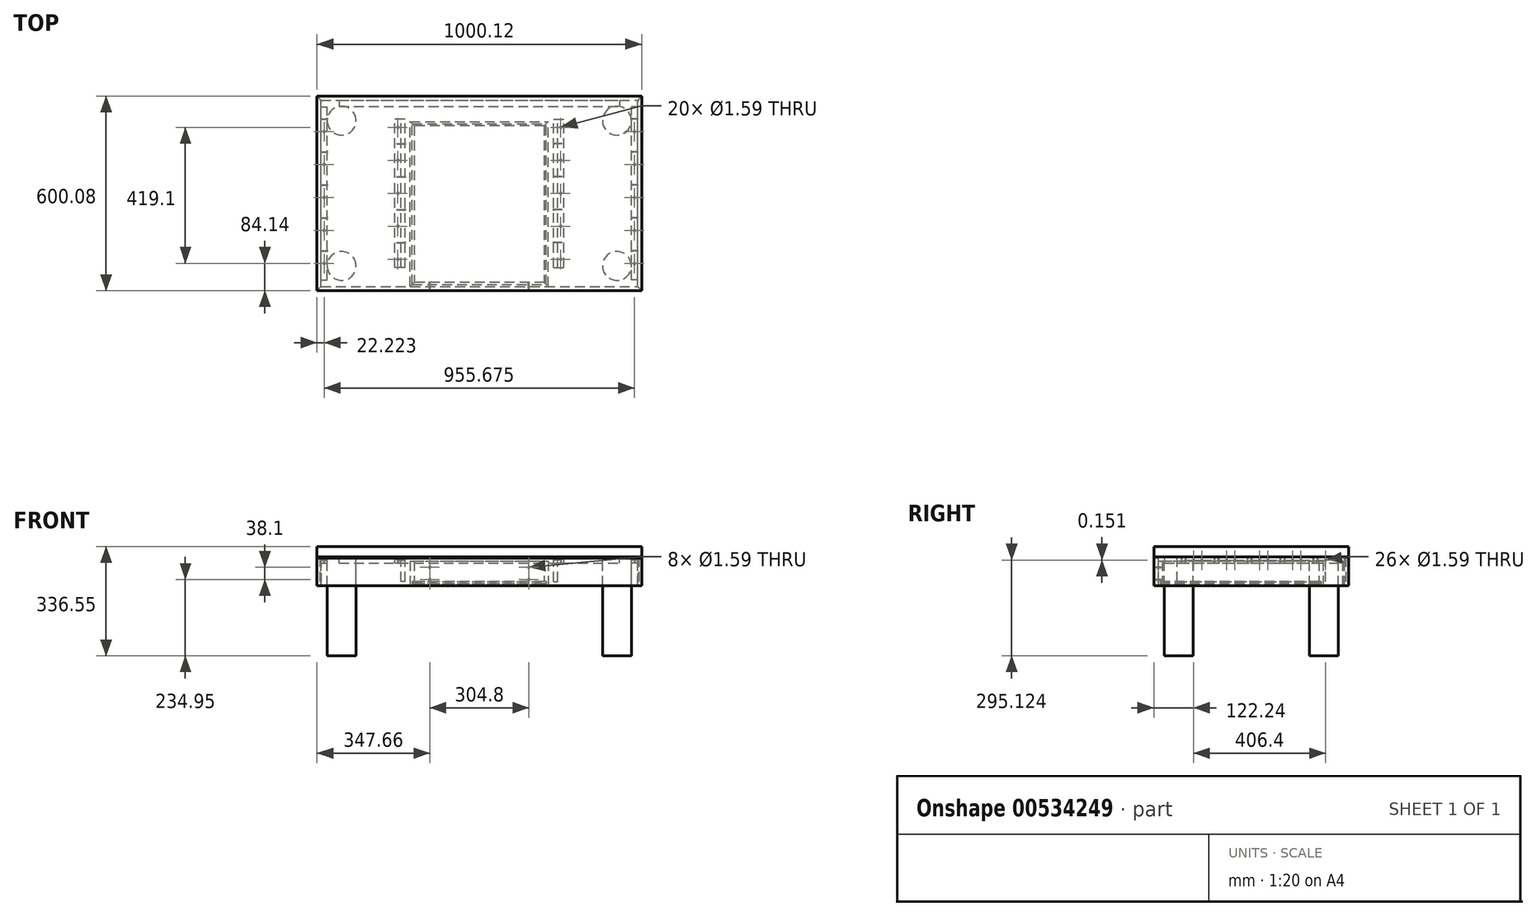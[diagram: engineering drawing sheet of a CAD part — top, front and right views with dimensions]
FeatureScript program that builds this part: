
annotation { "Feature Type Name" : "Feature", "Feature Type Description" : "" }
export const myFeature = defineFeature(function(context is Context, id is Id, definition is map)
    precondition{}
    {
        {
            var Q0;
            Q0=qCreatedBy(makeId("Top.planeOp"),FACE);
            var sketch = newSketch(context, id + "F0", { "sketchPlane" : qUnion([Q0])});
            skLineSegment(sketch, "E0.bottom", {"start": v(-500.06, 300.04) * mm, "end": v(500.06, 300.04) * mm});
            skLineSegment(sketch, "E0.top", {"start": v(-500.06, -300.04) * mm, "end": v(500.06, -300.04) * mm});
            skLineSegment(sketch, "E0.left", {"start": v(-500.06, 300.04) * mm, "end": v(-500.06, -300.04) * mm});
            skLineSegment(sketch, "E0.right", {"start": v(500.06, 300.04) * mm, "end": v(500.06, -300.04) * mm});
            skSolve(sketch);
        }
        {
            var Q0;
            Q0=makeQuery(id+"F0.imprint","IMPRINT",FACE,{"disambiguationData":[TD([[makeQuery(id+"F0.imprint","IMPRINT",EDGE,{"derivedFrom":sQuery(id+"F0.wireOp",EDGE,"E0.bottom")}),-1.0]])]});
            extrude(context, id + "F1", {"entities" : qUnion([Q0]), "depth" : 31.75 * mm, "offsetDistance" : 25.4 * mm});
        }
        {
            var Q0;
            Q0=makeQuery(id+"F1.opExtrude","CAP_FACE",FACE,{"disambiguationData":[OSD([sQuery(id+"F0.wireOp",EDGE,"E0.bottom"),sQuery(id+"F0.wireOp",EDGE,"E0.top"),sQuery(id+"F0.wireOp",EDGE,"E0.left"),sQuery(id+"F0.wireOp",EDGE,"E0.right")])],"isStart":true});
            var sketch = newSketch(context, id + "F2", { "sketchPlane" : qUnion([Q0])});
            skCircle(sketch, "E1", {"center": v(-423.86, 223.84) * mm, "radius": 44.45 * mm});
            skLineSegment(sketch, "E2", {"start": v(-423.86, 223.84) * mm, "end": v(-500.06, 223.84) * mm, "construction": true});
            skLineSegment(sketch, "E3", {"start": v(-423.86, 223.84) * mm, "end": v(-423.86, 300.04) * mm, "construction": true});
            skCircle(sketch, "E4", {"center": v(-423.86, -223.84) * mm, "radius": 44.45 * mm});
            skCircle(sketch, "E5", {"center": v(423.86, -223.84) * mm, "radius": 44.45 * mm});
            skCircle(sketch, "E6", {"center": v(423.86, 223.84) * mm, "radius": 44.45 * mm});
            skLineSegment(sketch, "E7", {"start": v(423.86, 223.84) * mm, "end": v(423.86, 300.04) * mm, "construction": true});
            skLineSegment(sketch, "E8", {"start": v(423.86, 223.84) * mm, "end": v(500.06, 223.84) * mm, "construction": true});
            skLineSegment(sketch, "E9", {"start": v(423.86, -223.84) * mm, "end": v(500.06, -223.84) * mm, "construction": true});
            skLineSegment(sketch, "E10", {"start": v(-500.06, -223.84) * mm, "end": v(-423.86, -223.84) * mm, "construction": true});
            skLineSegment(sketch, "E11", {"start": v(-423.86, -300.04) * mm, "end": v(-423.86, -223.84) * mm, "construction": true});
            skLineSegment(sketch, "E12", {"start": v(423.86, -223.84) * mm, "end": v(423.86, -300.04) * mm, "construction": true});
            skSolve(sketch);
        }
        {
            var Q0;
            Q0=makeQuery(id+"F2.imprint","IMPRINT",FACE,{"disambiguationData":[TD([[makeQuery(id+"F2.imprint","IMPRINT",EDGE,{"derivedFrom":sQuery(id+"F2.wireOp",EDGE,"E1")}),1.0]])]});
            var Q1;
            Q1=makeQuery(id+"F2.imprint","IMPRINT",FACE,{"disambiguationData":[TD([[makeQuery(id+"F2.imprint","IMPRINT",EDGE,{"derivedFrom":sQuery(id+"F2.wireOp",EDGE,"E6")}),1.0]])]});
            var Q2;
            Q2=makeQuery(id+"F2.imprint","IMPRINT",FACE,{"disambiguationData":[TD([[makeQuery(id+"F2.imprint","IMPRINT",EDGE,{"derivedFrom":sQuery(id+"F2.wireOp",EDGE,"E5")}),1.0]])]});
            var Q3;
            Q3=makeQuery(id+"F2.imprint","IMPRINT",FACE,{"disambiguationData":[TD([[makeQuery(id+"F2.imprint","IMPRINT",EDGE,{"derivedFrom":sQuery(id+"F2.wireOp",EDGE,"E4")}),1.0]])]});
            extrude(context, id + "F3", {"entities" : qUnion([Q0, Q1, Q2, Q3]), "operationType" : NewBodyOperationType.ADD, "depth" : 304.8 * mm, "offsetDistance" : 25.4 * mm});
        }
        {
            var Q0;
            Q0=makeQuery(id+"F1.opExtrude","CAP_FACE",FACE,{"disambiguationData":[OSD([sQuery(id+"F0.wireOp",EDGE,"E0.bottom"),sQuery(id+"F0.wireOp",EDGE,"E0.top"),sQuery(id+"F0.wireOp",EDGE,"E0.left"),sQuery(id+"F0.wireOp",EDGE,"E0.right")])],"isStart":true});
            var sketch = newSketch(context, id + "F4", { "sketchPlane" : qUnion([Q0])});
            skLineSegment(sketch, "E13.bottom", {"start": v(-500.06, 300.04) * mm, "end": v(-487.36, 300.04) * mm});
            skLineSegment(sketch, "E13.left", {"start": v(-500.06, 300.04) * mm, "end": v(-500.06, -300.04) * mm});
            skLineSegment(sketch, "E13.right", {"start": v(-487.36, 300.04) * mm, "end": v(-487.36, -287.34) * mm});
            skLineSegment(sketch, "E14.bottom", {"start": v(-487.36, 266.7) * mm, "end": v(-468.31, 266.7) * mm});
            skLineSegment(sketch, "E14.top", {"start": v(-487.36, -266.7) * mm, "end": v(-468.31, -266.7) * mm});
            skLineSegment(sketch, "E14.left", {"start": v(-487.36, 266.7) * mm, "end": v(-487.36, -266.7) * mm});
            skLineSegment(sketch, "E14.right", {"start": v(-468.31, 266.7) * mm, "end": v(-468.31, -266.7) * mm});
            skLineSegment(sketch, "E15.bottom", {"start": v(-228.6, 228.6) * mm, "end": v(-241.3, 228.6) * mm});
            skLineSegment(sketch, "E15.top", {"start": v(-228.6, -228.6) * mm, "end": v(-241.3, -228.6) * mm});
            skLineSegment(sketch, "E15.left", {"start": v(-228.6, 228.6) * mm, "end": v(-228.6, -228.6) * mm});
            skLineSegment(sketch, "E15.right", {"start": v(-241.3, 228.6) * mm, "end": v(-241.3, -228.6) * mm});
            skLineSegment(sketch, "E16.bottom", {"start": v(-241.3, 228.6) * mm, "end": v(-260.35, 228.6) * mm});
            skLineSegment(sketch, "E16.top", {"start": v(-241.3, -228.6) * mm, "end": v(-260.35, -228.6) * mm});
            skLineSegment(sketch, "E16.right", {"start": v(-260.35, 228.6) * mm, "end": v(-260.35, -228.6) * mm});
            skLineSegment(sketch, "E17.bottom", {"start": v(-500.06, -300.04) * mm, "end": v(500.06, -300.04) * mm});
            skLineSegment(sketch, "E17.top", {"start": v(-487.36, -287.34) * mm, "end": v(487.36, -287.34) * mm});
            skLineSegment(sketch, "E18", {"start": v(-500.06, -300.04) * mm, "end": v(-487.36, -287.34) * mm});
            skLineSegment(sketch, "E19", {"start": v(500.06, -300.04) * mm, "end": v(487.36, -287.34) * mm});
            skSolve(sketch);
        }
        {
            var Q0;
            Q0=makeQuery(id+"F4.imprint","IMPRINT",FACE,{"disambiguationData":[TD([[makeQuery(id+"F4.imprint","IMPRINT",EDGE,{"derivedFrom":sQuery(id+"F4.wireOp",EDGE,"E13.bottom")}),-1.0]])]});
            extrude(context, id + "F5", {"entities" : qUnion([Q0]), "depth" : 88.9 * mm, "offsetDistance" : 25.4 * mm});
        }
        {
            var Q0;
            Q0=makeQuery(id+"F4.imprint","IMPRINT",FACE,{"disambiguationData":[TD([[makeQuery(id+"F4.imprint","IMPRINT",EDGE,{"derivedFrom":sQuery(id+"F4.wireOp",EDGE,"E14.bottom")}),-1.0]])]});
            extrude(context, id + "F6", {"entities" : qUnion([Q0]), "depth" : 19.05 * mm, "offsetDistance" : 25.4 * mm});
        }
        {
            var Q0;
            Q0=makeQuery(id+"F4.imprint","IMPRINT",FACE,{"disambiguationData":[TD([[makeQuery(id+"F4.imprint","IMPRINT",EDGE,{"derivedFrom":sQuery(id+"F4.wireOp",EDGE,"E17.bottom")}),1.0]])]});
            extrude(context, id + "F7", {"entities" : qUnion([Q0]), "depth" : 88.9 * mm, "offsetDistance" : 25.4 * mm});
        }
        {
            var Q0;
            Q0=makeQuery(id+"F4.imprint","IMPRINT",FACE,{"disambiguationData":[TD([[makeQuery(id+"F4.imprint","IMPRINT",EDGE,{"derivedFrom":sQuery(id+"F4.wireOp",EDGE,"E16.bottom")}),1.0]])]});
            extrude(context, id + "F8", {"entities" : qUnion([Q0]), "depth" : 19.05 * mm, "offsetDistance" : 25.4 * mm});
        }
        {
            var Q0;
            {var subQ1=sQuery(id+"F4.wireOp",EDGE,"E15.bottom");Q0=makeQuery(id+"F4.imprint","IMPRINT",FACE,{"disambiguationData":[TD([[makeQuery(id+"F4.imprint","IMPRINT",EDGE,{"derivedFrom":subQ1}),1.0]])]});}
            var Q1;
            Q1=makeQuery(id+"F5.opExtrude","CAP_FACE",FACE,{"disambiguationData":[OSD([sQuery(id+"F4.wireOp",EDGE,"E13.bottom"),sQuery(id+"F4.wireOp",EDGE,"E13.top"),sQuery(id+"F4.wireOp",EDGE,"E13.left"),sQuery(id+"F4.wireOp",EDGE,"E13.right"),sQuery(id+"F4.wireOp",EDGE,"E14.left")])],"isStart":false});
            extrude(context, id + "F9", {"entities" : qUnion([Q0]), "endBound" : BoundingType.UP_TO_SURFACE, "depth" : 69.85 * mm, "endBoundEntityFace" : qUnion([Q1]), "hasOffset" : true, "offsetDistance" : 12.7 * mm});
        }
        {
            var Q0;
            Q0=makeQuery(id+"F8.opExtrude","CAP_FACE",FACE,{"disambiguationData":[OSD([sQuery(id+"F4.wireOp",EDGE,"E16.bottom"),sQuery(id+"F4.wireOp",EDGE,"E16.top"),sQuery(id+"F4.wireOp",EDGE,"E15.right"),sQuery(id+"F4.wireOp",EDGE,"E16.right")])],"isStart":false});
            var sketch = newSketch(context, id + "F10", { "sketchPlane" : qUnion([Q0])});
            skPoint(sketch, "E20", {"position": v(-250.83, -203.2) * mm});
            skPoint(sketch, "E20.positionSnap0", {"position": v(-250.83, -228.6) * mm});
            skPoint(sketch, "E21.0.1.0", {"position": v(-250.83, -101.6) * mm});
            skPoint(sketch, "E21.0.2.0", {"position": v(-250.83, 0) * mm});
            skPoint(sketch, "E21.0.3.0", {"position": v(-250.83, 101.6) * mm});
            skLineSegment(sketch, "E21.direction1", {"start": v(-250.83, -203.2) * mm, "end": v(-225.43, -203.2) * mm, "construction": true});
            skLineSegment(sketch, "E21.direction2", {"start": v(-250.83, -203.2) * mm, "end": v(-250.83, -101.6) * mm, "construction": true});
            skPoint(sketch, "E22.0.0.4", {"position": v(-250.83, 203.2) * mm});
            skSolve(sketch);
        }
        {
            var Q0;
            Q0=makeQuery(id+"F9.opExtrude","SWEPT_FACE",FACE,{"disambiguationData":[OSD([sQuery(id+"F4.wireOp",EDGE,"E15.left")])]});
            var sketch = newSketch(context, id + "F11", { "sketchPlane" : qUnion([Q0])});
            skLineSegment(sketch, "E23", {"start": v(228.6, -9.68) * mm, "end": v(-228.6, -9.68) * mm, "construction": true});
            skPoint(sketch, "E24", {"position": v(152.4, -9.68) * mm});
            skPoint(sketch, "E25.1.0.0", {"position": v(50.8, -9.68) * mm});
            skPoint(sketch, "E25.2.0.0", {"position": v(-50.8, -9.68) * mm});
            skPoint(sketch, "E25.3.0.0", {"position": v(-152.4, -9.68) * mm});
            skLineSegment(sketch, "E25.direction1", {"start": v(152.4, -9.68) * mm, "end": v(50.8, -9.68) * mm, "construction": true});
            skSolve(sketch);
        }
        {
            var Q0;
            Q0=makeQuery(id+"F6.opExtrude","CAP_FACE",FACE,{"disambiguationData":[OSD([sQuery(id+"F4.wireOp",EDGE,"E14.bottom"),sQuery(id+"F4.wireOp",EDGE,"E14.top"),sQuery(id+"F4.wireOp",EDGE,"E14.left"),sQuery(id+"F4.wireOp",EDGE,"E14.right")])],"isStart":false});
            var sketch = newSketch(context, id + "F12", { "sketchPlane" : qUnion([Q0])});
            skPoint(sketch, "E26", {"position": v(-477.84, -190.5) * mm});
            skPoint(sketch, "E26.positionSnap0", {"position": v(-477.84, -266.7) * mm});
            skPoint(sketch, "E27.0.1.0", {"position": v(-477.84, -88.9) * mm});
            skPoint(sketch, "E27.0.2.0", {"position": v(-477.84, 12.7) * mm});
            skPoint(sketch, "E27.0.3.0", {"position": v(-477.84, 114.3) * mm});
            skPoint(sketch, "E27.0.4.0", {"position": v(-477.84, 215.9) * mm});
            skLineSegment(sketch, "E27.direction1", {"start": v(-477.84, -266.7) * mm, "end": v(-452.44, -266.7) * mm, "construction": true});
            skLineSegment(sketch, "E27.direction2", {"start": v(-477.84, -266.7) * mm, "end": v(-477.84, -114.3) * mm, "construction": true});
            skSolve(sketch);
        }
        {
            var Q0;
            Q0=makeQuery(id+"F6.opExtrude","SWEPT_FACE",FACE,{"disambiguationData":[OSD([sQuery(id+"F4.wireOp",EDGE,"E14.right")])]});
            var sketch = newSketch(context, id + "F13", { "sketchPlane" : qUnion([Q0])});
            skPoint(sketch, "E28", {"position": v(228.6, -9.52) * mm});
            skPoint(sketch, "E28.positionSnap0", {"position": v(266.7, -9.53) * mm});
            skPoint(sketch, "E29.1.0.0", {"position": v(127, -9.53) * mm});
            skPoint(sketch, "E29.2.0.0", {"position": v(25.4, -9.53) * mm});
            skPoint(sketch, "E29.3.0.0", {"position": v(-76.2, -9.53) * mm});
            skPoint(sketch, "E29.4.0.0", {"position": v(-177.8, -9.53) * mm});
            skLineSegment(sketch, "E29.direction1", {"start": v(228.6, -9.53) * mm, "end": v(127, -9.53) * mm, "construction": true});
            skSolve(sketch);
        }
        {
            var Q0;
            Q0=sQuery(id+"F10.wireOp",VERTEX,"E20");
            var Q1;
            Q1=sQuery(id+"F10.wireOp",VERTEX,"E21.0.1.0");
            var Q2;
            Q2=sQuery(id+"F10.wireOp",VERTEX,"E21.0.2.0");
            var Q3;
            Q3=sQuery(id+"F10.wireOp",VERTEX,"E21.0.3.0");
            var Q4;
            Q4=sQuery(id+"F10.wireOp",VERTEX,"E21.0.4.0");
            var Q5;
            Q5=sQuery(id+"F10.wireOp",VERTEX,"E21.0.5.0");
            var Q6;
            Q6=sQuery(id+"F10.wireOp",VERTEX,"E21.0.6.0");
            var Q7;
            Q7=sQuery(id+"F10.wireOp",VERTEX,"E21.0.7.0");
            var Q8;
            Q8=sQuery(id+"F10.wireOp",VERTEX,"E21.0.8.0");
            var Q9;
            Q9=sQuery(id+"F11.wireOp",VERTEX,"E24");
            var Q10;
            Q10=sQuery(id+"F11.wireOp",VERTEX,"E25.1.0.0");
            var Q11;
            Q11=sQuery(id+"F11.wireOp",VERTEX,"E25.2.0.0");
            var Q12;
            Q12=sQuery(id+"F11.wireOp",VERTEX,"E25.3.0.0");
            var Q13;
            Q13=sQuery(id+"F11.wireOp",VERTEX,"E25.4.0.0");
            var Q14;
            Q14=sQuery(id+"F11.wireOp",VERTEX,"E25.5.0.0");
            var Q15;
            Q15=sQuery(id+"F11.wireOp",VERTEX,"E25.6.0.0");
            var Q16;
            Q16=sQuery(id+"F11.wireOp",VERTEX,"E25.7.0.0");
            var Q17;
            Q17=sQuery(id+"F10.wireOp",VERTEX,"E22.0.0.4");
            var Q18;
            Q18=sQuery(id+"F12.wireOp",VERTEX,"E26");
            var Q19;
            Q19=sQuery(id+"F12.wireOp",VERTEX,"E27.0.1.0");
            var Q20;
            Q20=sQuery(id+"F12.wireOp",VERTEX,"E27.0.2.0");
            var Q21;
            Q21=sQuery(id+"F12.wireOp",VERTEX,"E27.0.3.0");
            var Q22;
            Q22=sQuery(id+"F12.wireOp",VERTEX,"E27.0.4.0");
            var Q23;
            Q23=sQuery(id+"F13.wireOp",VERTEX,"cb4e85ae-bc8c-472d-8e2a-263fc974a90b.0.6.0");
            var Q24;
            Q24=sQuery(id+"F13.wireOp",VERTEX,"E29.5.0.0");
            var Q25;
            Q25=sQuery(id+"F13.wireOp",VERTEX,"E29.4.0.0");
            var Q26;
            Q26=sQuery(id+"F13.wireOp",VERTEX,"E29.3.0.0");
            var Q27;
            Q27=sQuery(id+"F13.wireOp",VERTEX,"E29.2.0.0");
            var Q28;
            Q28=sQuery(id+"F13.wireOp",VERTEX,"E29.1.0.0");
            var Q29;
            Q29=sQuery(id+"F13.wireOp",VERTEX,"E28");
            var Q30;
            Q30=makeQuery(id+"F8.opExtrude","SWEPT_BODY",BODY,{"disambiguationData":[OSD([sQuery(id+"F4.wireOp",EDGE,"E16.bottom"),sQuery(id+"F4.wireOp",EDGE,"E16.top"),sQuery(id+"F4.wireOp",EDGE,"E15.right"),sQuery(id+"F4.wireOp",EDGE,"E16.right")])]});
            var Q31;
            Q31=makeQuery(id+"F9.opExtrude","SWEPT_BODY",BODY,{"disambiguationData":[OSD([sQuery(id+"F4.wireOp",EDGE,"E15.bottom"),sQuery(id+"F4.wireOp",EDGE,"E15.top"),sQuery(id+"F4.wireOp",EDGE,"E15.left"),sQuery(id+"F4.wireOp",EDGE,"E15.right")])]});
            var Q32;
            Q32=makeQuery(id+"F6.opExtrude","SWEPT_BODY",BODY,{"disambiguationData":[OSD([sQuery(id+"F4.wireOp",EDGE,"E14.bottom"),sQuery(id+"F4.wireOp",EDGE,"E14.top"),sQuery(id+"F4.wireOp",EDGE,"E14.left"),sQuery(id+"F4.wireOp",EDGE,"E14.right")])]});
            hole(context, id + "F14", {"style" : HoleStyle.C_SINK, "endStyle" : HoleEndStyle.BLIND, "holeDiameter" : 1.59 * mm, "cSinkDiameter" : 6.35 * mm, "cSinkAngle" : 90 * degree, "majorDiameter" : 6.35 * mm, "holeDepth" : 25.4 * mm, "isTappedThrough" : true, "tappedDepth" : 12.7 * mm, "tapClearance" : 3, "locations" : qUnion([Q0, Q1, Q2, Q3, Q4, Q5, Q6, Q7, Q8, Q9, Q10, Q11, Q12, Q13, Q14, Q15, Q16, Q17, Q18, Q19, Q20, Q21, Q22, Q23, Q24, Q25, Q26, Q27, Q28, Q29]), "scope" : qUnion([Q30, Q31, Q32])});
        }
        {
            var Q0;
            Q0=makeQuery(id+"F5.opExtrude","SWEPT_EDGE",EDGE,{"disambiguationData":[OSD([sQuery(id+"F0.wireOp",EDGE,"E0.top"),sQuery(id+"F4.wireOp",EDGE,"E13.bottom"),sQuery(id+"F4.wireOp",EDGE,"E13.right")])]});
            var Q1;
            Q1=makeQuery(id+"F5.opExtrude","SWEPT_EDGE",EDGE,{"disambiguationData":[OSD([sQuery(id+"F0.wireOp",EDGE,"E0.bottom"),sQuery(id+"F4.wireOp",EDGE,"E13.top"),sQuery(id+"F4.wireOp",EDGE,"E13.right")])]});
            chamfer(context, id + "F15", {"entities" : qUnion([Q0, Q1]), "width" : 12.7 * mm, "tangentPropagation" : true});
        }
        {
            var Q0;
            Q0=makeQuery(id+"F5.opExtrude","SWEPT_BODY",BODY,{"disambiguationData":[OSD([sQuery(id+"F4.wireOp",EDGE,"E13.bottom"),sQuery(id+"F4.wireOp",EDGE,"E13.top"),sQuery(id+"F4.wireOp",EDGE,"E13.left"),sQuery(id+"F4.wireOp",EDGE,"E13.right")])]});
            var Q1;
            Q1=makeQuery(id+"F6.opExtrude","SWEPT_BODY",BODY,{"disambiguationData":[OSD([sQuery(id+"F4.wireOp",EDGE,"E14.bottom"),sQuery(id+"F4.wireOp",EDGE,"E14.top"),sQuery(id+"F4.wireOp",EDGE,"E14.left"),sQuery(id+"F4.wireOp",EDGE,"E14.right")])]});
            var Q2;
            Q2=makeQuery(id+"F9.opExtrude","SWEPT_BODY",BODY,{"disambiguationData":[OSD([sQuery(id+"F4.wireOp",EDGE,"E15.bottom"),sQuery(id+"F4.wireOp",EDGE,"E15.top"),sQuery(id+"F4.wireOp",EDGE,"E15.left"),sQuery(id+"F4.wireOp",EDGE,"E15.right")])]});
            var Q3;
            Q3=makeQuery(id+"F8.opExtrude","SWEPT_BODY",BODY,{"disambiguationData":[OSD([sQuery(id+"F4.wireOp",EDGE,"E16.bottom"),sQuery(id+"F4.wireOp",EDGE,"E16.top"),sQuery(id+"F4.wireOp",EDGE,"E15.right"),sQuery(id+"F4.wireOp",EDGE,"E16.right")])]});
            var Q4;
            Q4=qCreatedBy(makeId("Right.planeOp"),FACE);
            mirror(context, id + "F16", {"entities" : qUnion([Q0, Q1, Q2, Q3]), "mirrorPlane" : qUnion([Q4])});
        }
        {
            var Q0;
            Q0=makeQuery(id+"F5.opExtrude","CAP_FACE",FACE,{"disambiguationData":[OSD([sQuery(id+"F4.wireOp",EDGE,"E13.bottom"),sQuery(id+"F4.wireOp",EDGE,"E13.top"),sQuery(id+"F4.wireOp",EDGE,"E13.left"),sQuery(id+"F4.wireOp",EDGE,"E13.right"),sQuery(id+"F4.wireOp",EDGE,"E14.left")])],"isStart":false});
            var sketch = newSketch(context, id + "F17", { "sketchPlane" : qUnion([Q0])});
            skLineSegment(sketch, "E30.bottom", {"start": v(-500.06, 300.04) * mm, "end": v(500.06, 300.04) * mm});
            skLineSegment(sketch, "E30.top", {"start": v(-487.36, 287.34) * mm, "end": v(487.36, 287.34) * mm});
            skLineSegment(sketch, "E31", {"start": v(500.06, 300.04) * mm, "end": v(487.36, 287.34) * mm});
            skLineSegment(sketch, "E32", {"start": v(-500.06, 300.04) * mm, "end": v(-487.36, 287.34) * mm});
            skSolve(sketch);
        }
        {
            var Q0;
            Q0=makeQuery(id+"F17.imprint","IMPRINT",FACE,{"disambiguationData":[TD([[makeQuery(id+"F17.imprint","IMPRINT",EDGE,{"derivedFrom":sQuery(id+"F17.wireOp",EDGE,"E30.bottom")}),-1.0]])]});
            var Q1;
            Q1=makeQuery(id+"F1.opExtrude","CAP_FACE",FACE,{"disambiguationData":[OSD([sQuery(id+"F0.wireOp",EDGE,"E0.bottom"),sQuery(id+"F0.wireOp",EDGE,"E0.top"),sQuery(id+"F0.wireOp",EDGE,"E0.left"),sQuery(id+"F0.wireOp",EDGE,"E0.right")])],"isStart":true});
            extrude(context, id + "F18", {"entities" : qUnion([Q0]), "endBound" : BoundingType.UP_TO_SURFACE, "oppositeDirection" : true, "depth" : 25.4 * mm, "endBoundEntityFace" : qUnion([Q1]), "hasOffset" : true, "offsetDistance" : 3.17 * mm});
        }
        {
            var Q0;
            Q0=makeQuery(id+"F9.opExtrude","CAP_FACE",FACE,{"disambiguationData":[OSD([sQuery(id+"F4.wireOp",EDGE,"E15.bottom"),sQuery(id+"F4.wireOp",EDGE,"E15.top"),sQuery(id+"F4.wireOp",EDGE,"E15.left"),sQuery(id+"F4.wireOp",EDGE,"E15.right")])],"isStart":false});
            cPlane(context, id + "F19", {"entities" : qUnion([Q0]), "cplaneType" : CPlaneType.OFFSET, "offset" : 12.7 * mm, "width" : 152.4 * mm, "height" : 152.4 * mm});
        }
        {
            var Q0;
            Q0=qCreatedBy(id+"F19.planeOp",FACE);
            var sketch = newSketch(context, id + "F20", { "sketchPlane" : qUnion([Q0])});
            skLineSegment(sketch, "E33.bottom", {"start": v(-212.73, 287.34) * mm, "end": v(212.73, 287.34) * mm});
            skLineSegment(sketch, "E33.top", {"start": v(-212.72, -220.66) * mm, "end": v(212.72, -220.66) * mm});
            skLineSegment(sketch, "E33.left", {"start": v(-212.73, 287.34) * mm, "end": v(-212.72, -220.66) * mm});
            skLineSegment(sketch, "E33.right", {"start": v(212.73, 287.34) * mm, "end": v(212.73, -220.66) * mm});
            skLineSegment(sketch, "E34.bottom", {"start": v(-200.03, 274.64) * mm, "end": v(200.03, 274.64) * mm});
            skLineSegment(sketch, "E34.top", {"start": v(-200.03, -207.96) * mm, "end": v(200.03, -207.96) * mm});
            skLineSegment(sketch, "E34.left", {"start": v(-200.03, 274.64) * mm, "end": v(-200.03, -207.96) * mm});
            skLineSegment(sketch, "E34.right", {"start": v(200.03, 274.64) * mm, "end": v(200.03, -207.96) * mm});
            skLineSegment(sketch, "E35", {"start": v(-212.73, 287.34) * mm, "end": v(-200.03, 274.64) * mm});
            skLineSegment(sketch, "E36", {"start": v(200.03, 274.64) * mm, "end": v(212.73, 287.34) * mm});
            skLineSegment(sketch, "E37", {"start": v(200.03, -207.96) * mm, "end": v(212.73, -220.66) * mm});
            skLineSegment(sketch, "E38", {"start": v(-200.03, -207.96) * mm, "end": v(-212.73, -220.66) * mm});
            skSolve(sketch);
        }
        {
            var Q0;
            Q0=makeQuery(id+"F20.imprint","IMPRINT",FACE,{"disambiguationData":[TD([[makeQuery(id+"F20.imprint","IMPRINT",EDGE,{"derivedFrom":sQuery(id+"F20.wireOp",EDGE,"E33.bottom")}),-1.0]])]});
            var Q1;
            Q1=makeQuery(id+"F1.opExtrude","CAP_FACE",FACE,{"disambiguationData":[OSD([sQuery(id+"F0.wireOp",EDGE,"E0.bottom"),sQuery(id+"F0.wireOp",EDGE,"E0.top"),sQuery(id+"F0.wireOp",EDGE,"E0.left"),sQuery(id+"F0.wireOp",EDGE,"E0.right")])],"isStart":true});
            extrude(context, id + "F21", {"entities" : qUnion([Q0]), "endBound" : BoundingType.UP_TO_SURFACE, "oppositeDirection" : true, "depth" : 88.9 * mm, "endBoundEntityFace" : qUnion([Q1]), "hasOffset" : true, "offsetDistance" : 12.7 * mm});
        }
        {
            var Q0;
            Q0=makeQuery(id+"F20.imprint","IMPRINT",FACE,{"disambiguationData":[TD([[makeQuery(id+"F20.imprint","IMPRINT",EDGE,{"derivedFrom":sQuery(id+"F20.wireOp",EDGE,"E33.left")}),1.0]])]});
            var Q1;
            Q1=makeQuery(id+"F21.opExtrude","CAP_FACE",FACE,{"disambiguationData":[OSD([sQuery(id+"F20.wireOp",EDGE,"E33.bottom"),sQuery(id+"F20.wireOp",EDGE,"E34.bottom"),sQuery(id+"F20.wireOp",EDGE,"E35"),sQuery(id+"F20.wireOp",EDGE,"E36")])],"isStart":false});
            extrude(context, id + "F22", {"entities" : qUnion([Q0]), "endBound" : BoundingType.UP_TO_SURFACE, "oppositeDirection" : true, "depth" : 25.4 * mm, "endBoundEntityFace" : qUnion([Q1]), "offsetDistance" : 25.4 * mm});
        }
        {
            var Q0;
            Q0=makeQuery(id+"F20.imprint","IMPRINT",FACE,{"disambiguationData":[TD([[makeQuery(id+"F20.imprint","IMPRINT",EDGE,{"derivedFrom":sQuery(id+"F20.wireOp",EDGE,"E33.right")}),-1.0]])]});
            var Q1;
            Q1=makeQuery(id+"F21.opExtrude","CAP_FACE",FACE,{"disambiguationData":[OSD([sQuery(id+"F20.wireOp",EDGE,"E33.bottom"),sQuery(id+"F20.wireOp",EDGE,"E34.bottom"),sQuery(id+"F20.wireOp",EDGE,"E35"),sQuery(id+"F20.wireOp",EDGE,"E36")])],"isStart":false});
            extrude(context, id + "F23", {"entities" : qUnion([Q0]), "endBound" : BoundingType.UP_TO_SURFACE, "oppositeDirection" : true, "depth" : 25.4 * mm, "endBoundEntityFace" : qUnion([Q1]), "offsetDistance" : 25.4 * mm});
        }
        {
            var Q0;
            Q0=makeQuery(id+"F20.imprint","IMPRINT",FACE,{"disambiguationData":[TD([[makeQuery(id+"F20.imprint","IMPRINT",EDGE,{"derivedFrom":sQuery(id+"F20.wireOp",EDGE,"E33.top")}),1.0]])]});
            var Q1;
            {var subQ0=sQuery(id+"F20.wireOp",EDGE,"E36");Q1=qUnion([makeQuery(id+"F21.opExtrude","CAP_FACE",FACE,{"disambiguationData":[OSD([sQuery(id+"F20.wireOp",EDGE,"E33.bottom"),sQuery(id+"F20.wireOp",EDGE,"E34.bottom"),sQuery(id+"F20.wireOp",EDGE,"E35"),subQ0])],"isStart":false}),makeQuery(id+"F23.opExtrude","CAP_FACE",FACE,{"disambiguationData":[OSD([sQuery(id+"F20.wireOp",EDGE,"E33.right"),sQuery(id+"F20.wireOp",EDGE,"E34.right"),subQ0,sQuery(id+"F20.wireOp",EDGE,"E37")])],"isStart":false})]);}
            extrude(context, id + "F24", {"entities" : qUnion([Q0]), "endBound" : BoundingType.UP_TO_SURFACE, "oppositeDirection" : true, "depth" : 25.4 * mm, "endBoundEntityFace" : qUnion([Q1]), "offsetDistance" : 25.4 * mm});
        }
        {
            var Q0;
            Q0=makeQuery(id+"F1.opExtrude","CAP_FACE",FACE,{"disambiguationData":[OSD([sQuery(id+"F0.wireOp",EDGE,"E0.bottom"),sQuery(id+"F0.wireOp",EDGE,"E0.top"),sQuery(id+"F0.wireOp",EDGE,"E0.left"),sQuery(id+"F0.wireOp",EDGE,"E0.right")])],"isStart":true});
            var sketch = newSketch(context, id + "F25", { "sketchPlane" : qUnion([Q0])});
            skLineSegment(sketch, "E39.bottom", {"start": v(-431.8, -287.34) * mm, "end": v(431.8, -287.34) * mm});
            skLineSegment(sketch, "E39.top", {"start": v(-431.8, -268.29) * mm, "end": v(431.8, -268.29) * mm});
            skLineSegment(sketch, "E39.left", {"start": v(-431.8, -287.34) * mm, "end": v(-431.8, -268.29) * mm});
            skLineSegment(sketch, "E39.right", {"start": v(431.8, -287.34) * mm, "end": v(431.8, -268.29) * mm});
            skSolve(sketch);
        }
        {
            var Q0;
            Q0=makeQuery(id+"F25.imprint","IMPRINT",FACE,{"disambiguationData":[TD([[makeQuery(id+"F25.imprint","IMPRINT",EDGE,{"derivedFrom":sQuery(id+"F25.wireOp",EDGE,"E39.bottom")}),1.0]])]});
            extrude(context, id + "F26", {"entities" : qUnion([Q0]), "depth" : 19.05 * mm, "offsetDistance" : 25.4 * mm});
        }
        {
            var Q0;
            Q0=makeQuery(id+"F22.opExtrude","CAP_FACE",FACE,{"disambiguationData":[OSD([sQuery(id+"F20.wireOp",EDGE,"E33.left"),sQuery(id+"F20.wireOp",EDGE,"E34.left"),sQuery(id+"F20.wireOp",EDGE,"E35"),sQuery(id+"F20.wireOp",EDGE,"E38")])],"isStart":true});
            cPlane(context, id + "F27", {"entities" : qUnion([Q0]), "cplaneType" : CPlaneType.OFFSET, "offset" : 6.35 * mm, "oppositeDirection" : true, "width" : 152.4 * mm, "height" : 152.4 * mm});
        }
        {
            var Q0;
            Q0=qCreatedBy(id+"F27.planeOp",FACE);
            var sketch = newSketch(context, id + "F28", { "sketchPlane" : qUnion([Q0])});
            skLineSegment(sketch, "E40.bottom", {"start": v(-206.38, 280.99) * mm, "end": v(206.38, 280.99) * mm});
            skLineSegment(sketch, "E40.top", {"start": v(-206.38, -214.31) * mm, "end": v(206.38, -214.31) * mm});
            skLineSegment(sketch, "E40.left", {"start": v(-206.38, 280.99) * mm, "end": v(-206.38, -214.31) * mm});
            skLineSegment(sketch, "E40.right", {"start": v(206.38, 280.99) * mm, "end": v(206.38, -214.31) * mm});
            skSolve(sketch);
        }
        {
            var Q0;
            Q0 = qSketchRegion(id + "F28", true);
            extrude(context, id + "F29", {"entities" : qUnion([Q0]), "operationType" : NewBodyOperationType.REMOVE, "oppositeDirection" : true, "depth" : 6.35 * mm, "offsetDistance" : 25.4 * mm});
        }
        {
            var Q0;
            Q0=makeQuery(id+"F28.imprint","IMPRINT",FACE,{"disambiguationData":[TD([[makeQuery(id+"F28.imprint","IMPRINT",EDGE,{"derivedFrom":sQuery(id+"F28.wireOp",EDGE,"E40.bottom")}),-1.0]])]});
            extrude(context, id + "F30", {"entities" : qUnion([Q0]), "oppositeDirection" : true, "depth" : 6.35 * mm, "offsetDistance" : 25.4 * mm});
        }
        {
            var Q0;
            {var subQ0=sQuery(id+"F20.wireOp",EDGE,"E36");var subQ1=sQuery(id+"F20.wireOp",EDGE,"E35");var subQ2=sQuery(id+"F20.wireOp",EDGE,"E34.bottom");Q0=makeQuery(id+"F29.boolean.opBoolean","SPLIT",FACE,{"disambiguationData":[TD([makeQuery(id+"F21.opExtrude","CAP_FACE",FACE,{"disambiguationData":[OSD([sQuery(id+"F20.wireOp",EDGE,"E33.bottom"),subQ2,subQ1,subQ0])],"isStart":false})])],"derivedFrom":makeQuery(id+"F21.opExtrude","SWEPT_FACE",FACE,{"disambiguationData":[OSD([subQ2])]})});}
            var sketch = newSketch(context, id + "F31", { "sketchPlane" : qUnion([Q0])});
            skPoint(sketch, "E41", {"position": v(-152.4, -31.75) * mm});
            skPoint(sketch, "E42.0.1.0", {"position": v(-152.4, -69.85) * mm});
            skPoint(sketch, "E42.1.0.0", {"position": v(152.4, -31.75) * mm});
            skPoint(sketch, "E42.1.1.0", {"position": v(152.4, -69.85) * mm});
            skLineSegment(sketch, "E42.direction1", {"start": v(-152.4, -31.75) * mm, "end": v(152.4, -31.75) * mm, "construction": true});
            skLineSegment(sketch, "E42.direction2", {"start": v(-152.4, -31.75) * mm, "end": v(-152.4, -69.85) * mm, "construction": true});
            skSolve(sketch);
        }
        {
            var Q0;
            Q0=sQuery(id+"F31.wireOp",VERTEX,"E41");
            var Q1;
            Q1=sQuery(id+"F31.wireOp",VERTEX,"E42.0.1.0");
            var Q2;
            Q2=sQuery(id+"F31.wireOp",VERTEX,"E42.1.0.0");
            var Q3;
            Q3=sQuery(id+"F31.wireOp",VERTEX,"E42.1.1.0");
            var Q4;
            Q4=makeQuery(id+"F21.opExtrude","SWEPT_BODY",BODY,{"disambiguationData":[OSD([sQuery(id+"F20.wireOp",EDGE,"E33.bottom"),sQuery(id+"F20.wireOp",EDGE,"E34.bottom"),sQuery(id+"F20.wireOp",EDGE,"E35"),sQuery(id+"F20.wireOp",EDGE,"E36")])]});
            var Q5;
            Q5=makeQuery(id+"F18.opExtrude","SWEPT_BODY",BODY,{"disambiguationData":[OSD([sQuery(id+"F17.wireOp",EDGE,"E30.bottom"),sQuery(id+"F17.wireOp",EDGE,"E30.top"),sQuery(id+"F17.wireOp",EDGE,"E31"),sQuery(id+"F17.wireOp",EDGE,"E32")])]});
            hole(context, id + "F32", {"style" : HoleStyle.C_SINK, "endStyle" : HoleEndStyle.BLIND, "holeDiameter" : 1.59 * mm, "cSinkDiameter" : 6.35 * mm, "cSinkAngle" : 90 * degree, "majorDiameter" : 6.35 * mm, "holeDepth" : 19.05 * mm, "isTappedThrough" : true, "tappedDepth" : 12.7 * mm, "tapClearance" : 3, "locations" : qUnion([Q0, Q1, Q2, Q3]), "scope" : qUnion([Q4, Q5])});
        }
    });
